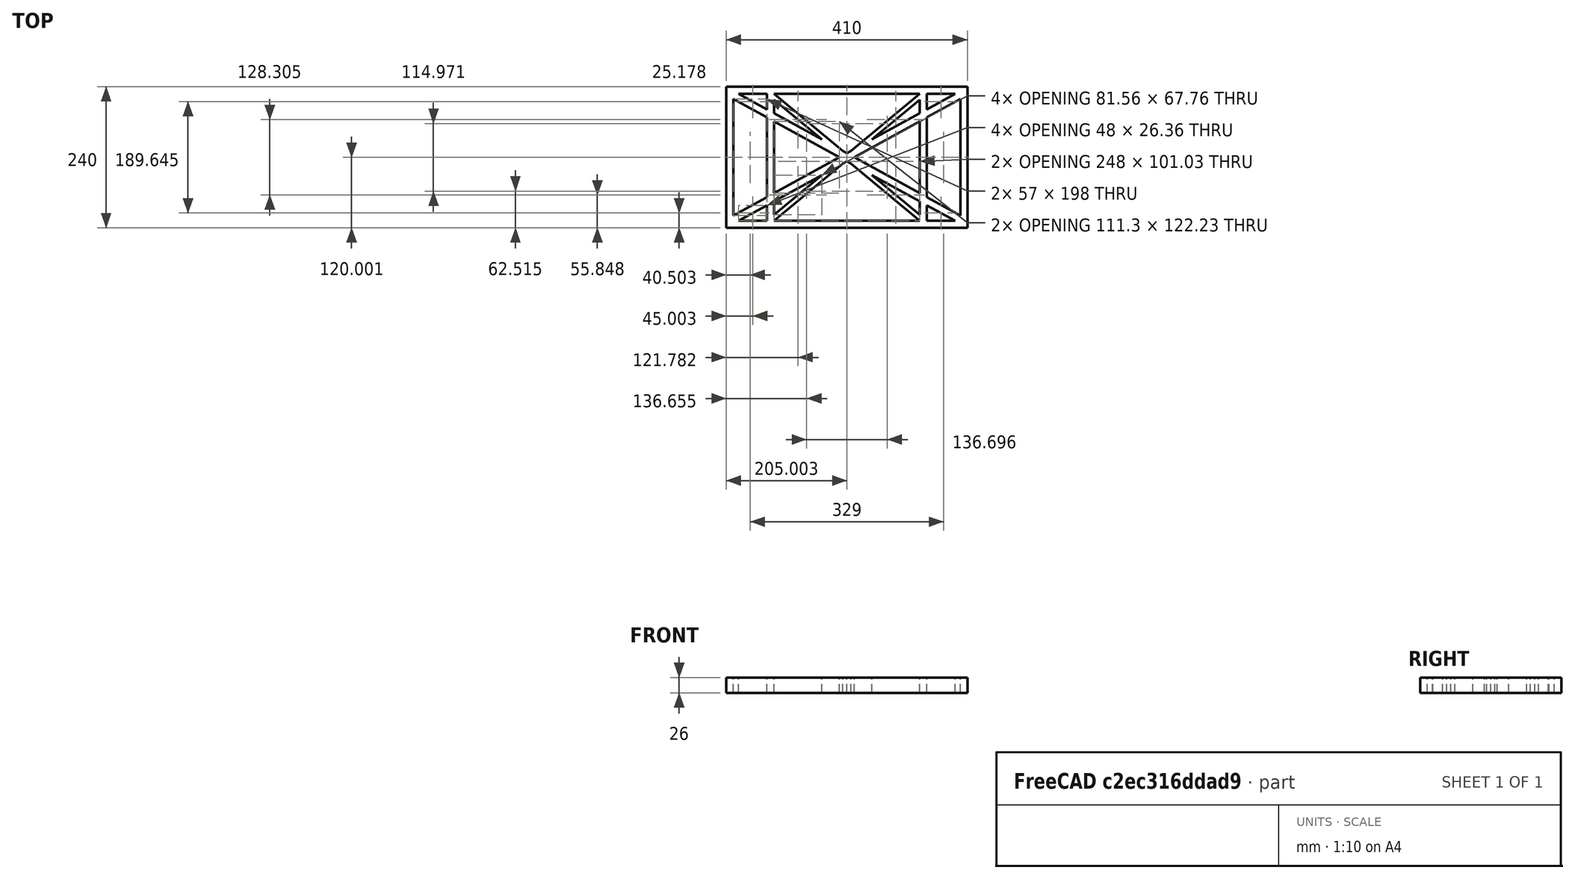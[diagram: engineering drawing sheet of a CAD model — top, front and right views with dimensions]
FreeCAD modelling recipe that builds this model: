
FCSTD DOCUMENT  (FreeCAD 0.19R0.19.2)
Label: laptopStand026
License: All rights reserved
LicenseURL: http://en.wikipedia.org/wiki/All_rights_reserved
objects: Sketcher::SketchObject×3, Part::Extrusion×1
note: 4 computed .brp shape members not serialized (recipe doc carries the construction recipe); baked Part::Feature solids carry a one-line shape summary decoded from their .brp

FEATURE [Sketcher::SketchObject] Sketch
  FullyConstrained = true
  sketch-geometry (52):
    g0: LineSegment StartX=-22.9272 StartY=136.221 StartZ=0 EndX=-22.9272 EndY=-103.779 EndZ=0
    g1: LineSegment StartX=-22.9272 StartY=136.221 StartZ=0 EndX=387.073 EndY=136.221 EndZ=0
    g2: LineSegment StartX=-22.9272 StartY=-103.779 StartZ=0 EndX=387.073 EndY=-103.779 EndZ=0
    g3: LineSegment StartX=387.073 StartY=136.221 StartZ=0 EndX=387.073 EndY=-103.779 EndZ=0
    g4: LineSegment StartX=375.073 StartY=115.221 StartZ=0 EndX=318.073 EndY=83.9235 EndZ=0
    g5: LineSegment StartX=-10.9272 StartY=-82.7794 StartZ=0 EndX=46.0728 EndY=-51.4823 EndZ=0
    g6: LineSegment StartX=-1.92719 StartY=124.221 StartZ=0 EndX=46.0728 EndY=97.8651 EndZ=0
    g7: LineSegment StartX=366.073 StartY=-91.7794 StartZ=0 EndX=318.073 EndY=-65.424 EndZ=0
    g8: LineSegment StartX=-10.9272 StartY=115.221 StartZ=0 EndX=-10.9272 EndY=-82.7794 EndZ=0
    g9: LineSegment StartX=375.073 StartY=-82.7794 StartZ=0 EndX=375.073 EndY=115.221 EndZ=0
    g10: LineSegment StartX=-1.92719 StartY=-91.7794 StartZ=0 EndX=46.0728 EndY=-91.7794 EndZ=0
    g11: LineSegment StartX=318.073 StartY=124.221 StartZ=0 EndX=366.073 EndY=124.221 EndZ=0
    g12: LineSegment StartX=306.073 StartY=-81.8102 StartZ=0 EndX=224.513 EndY=-14.0532 EndZ=0
    g13: LineSegment StartX=58.0728 StartY=114.251 StartZ=0 EndX=139.632 EndY=46.4944 EndZ=0
    g14: LineSegment StartX=306.073 StartY=124.221 StartZ=0 EndX=189.124 EndY=27.0628 EndZ=0
    g15: LineSegment StartX=58.0728 StartY=-91.7794 StartZ=0 EndX=175.022 EndY=5.37834 EndZ=0
    g16: LineSegment StartX=46.0728 StartY=124.221 StartZ=0 EndX=46.0728 EndY=97.8651 EndZ=0
    g17: LineSegment StartX=58.0728 StartY=-81.8102 StartZ=0 EndX=58.0728 EndY=-58.8351 EndZ=0
    g18: LineSegment StartX=318.073 StartY=124.221 StartZ=0 EndX=318.073 EndY=97.8651 EndZ=0
    g19: LineSegment StartX=306.073 StartY=114.251 StartZ=0 EndX=306.073 EndY=91.2763 EndZ=0
    g20: LineSegment StartX=182.073 StartY=23.1914 StartZ=0 EndX=189.124 EndY=27.0628 EndZ=0
    g21: LineSegment StartX=182.073 StartY=9.24976 StartZ=0 EndX=175.022 EndY=5.37834 EndZ=0
    g22: LineSegment StartX=224.513 StartY=46.4944 StartZ=0 EndX=306.073 EndY=114.251 EndZ=0
    g23: LineSegment StartX=175.022 StartY=27.0628 StartZ=0 EndX=58.0728 EndY=124.221 EndZ=0
    g24: LineSegment StartX=169.377 StartY=16.2206 StartZ=0 EndX=58.0728 EndY=77.3346 EndZ=0
    g25: LineSegment StartX=139.632 StartY=-14.0532 StartZ=0 EndX=58.0728 EndY=-81.8102 EndZ=0
    g26: LineSegment StartX=194.768 StartY=16.2206 StartZ=0 EndX=306.073 EndY=-44.8935 EndZ=0
    g27: LineSegment StartX=224.513 StartY=46.4944 StartZ=0 EndX=306.073 EndY=91.2763 EndZ=0
    g28: LineSegment StartX=175.022 StartY=27.0628 StartZ=0 EndX=182.073 EndY=23.1914 EndZ=0
    g29: LineSegment StartX=139.632 StartY=-14.0532 StartZ=0 EndX=58.0728 EndY=-58.8351 EndZ=0
    g30: LineSegment StartX=189.124 StartY=5.37834 StartZ=0 EndX=182.073 EndY=9.24976 EndZ=0
    g31: LineSegment StartX=189.124 StartY=5.37834 StartZ=0 EndX=306.073 EndY=-91.7794 EndZ=0
    g32: LineSegment StartX=306.073 StartY=77.3346 StartZ=0 EndX=306.073 EndY=-44.8935 EndZ=0
    g33: LineSegment StartX=318.073 StartY=83.9235 StartZ=0 EndX=318.073 EndY=-51.4823 EndZ=0
    g34: LineSegment StartX=318.073 StartY=97.8651 StartZ=0 EndX=366.073 EndY=124.221 EndZ=0
    g35: LineSegment StartX=306.073 StartY=77.3346 StartZ=0 EndX=194.768 EndY=16.2206 EndZ=0
    g36: LineSegment StartX=306.073 StartY=-58.8351 StartZ=0 EndX=224.513 EndY=-14.0532 EndZ=0
    g37: LineSegment StartX=306.073 StartY=-58.8351 StartZ=0 EndX=306.073 EndY=-81.8102 EndZ=0
    g38: LineSegment StartX=318.073 StartY=-51.4823 StartZ=0 EndX=375.073 EndY=-82.7794 EndZ=0
    g39: LineSegment StartX=318.073 StartY=-65.424 StartZ=0 EndX=318.073 EndY=-91.7794 EndZ=0
    g40: LineSegment StartX=306.073 StartY=124.221 StartZ=0 EndX=58.0728 EndY=124.221 EndZ=0
    g41: LineSegment StartX=318.073 StartY=-91.7794 StartZ=0 EndX=366.073 EndY=-91.7794 EndZ=0
    g42: LineSegment StartX=58.0728 StartY=-91.7794 StartZ=0 EndX=306.073 EndY=-91.7794 EndZ=0
    g43: LineSegment StartX=58.0728 StartY=-44.8935 StartZ=0 EndX=58.0728 EndY=77.3346 EndZ=0
    g44: LineSegment StartX=46.0728 StartY=-65.424 StartZ=0 EndX=-1.92719 EndY=-91.7794 EndZ=0
    g45: LineSegment StartX=46.0728 StartY=-65.424 StartZ=0 EndX=46.0728 EndY=-91.7794 EndZ=0
    g46: LineSegment StartX=58.0728 StartY=-44.8935 StartZ=0 EndX=169.377 EndY=16.2206 EndZ=0
    g47: LineSegment StartX=58.0728 StartY=91.2763 StartZ=0 EndX=58.0728 EndY=114.251 EndZ=0
    g48: LineSegment StartX=46.0728 StartY=83.9235 StartZ=0 EndX=46.0728 EndY=-51.4823 EndZ=0
    g49: LineSegment StartX=46.0728 StartY=124.221 StartZ=0 EndX=-1.92719 EndY=124.221 EndZ=0
    g50: LineSegment StartX=58.0728 StartY=91.2763 StartZ=0 EndX=139.632 EndY=46.4944 EndZ=0
    g51: LineSegment StartX=46.0728 StartY=83.9235 StartZ=0 EndX=-10.9272 EndY=115.221 EndZ=0
  constraints (102):
    c: Vertical(g0)
    c: Distance(g0) = 240
    c: Horizontal(g1)
    c: Distance(g1) = 410
    c: Coincident(g1,g0)
    c: Coincident(g2,g0)
    c: Horizontal(g2)
    c: Coincident(g3,g1)
    c: Vertical(g3)
    c: Coincident(g2,g3)
    c: Block(g1)
    c: Horizontal(g10)
    c: Horizontal(g11)
    c: PointOnObject(g35,g6)
    c: Coincident(g28,g20)
    c: Coincident(g30,g21)
    c: Tangent(g7,g24)
    c: PointOnObject(g24,g5)
    c: PointOnObject(g26,g4)
    c: Coincident(g20,g14)
    c: Tangent(g20,g27)
    c: Coincident(g50,g13)
    c: Coincident(g28,g23)
    c: Coincident(g22,g27)
    c: Coincident(g21,g15)
    c: Coincident(g29,g25)
    c: Tangent(g21,g29)
    c: Coincident(g36,g12)
    c: Coincident(g31,g30)
    c: Coincident(g22,g19)
    c: Tangent(g19,g32)
    c: Tangent(g18,g33)
    c: Coincident(g27,g19)
    c: Tangent(g27,g34)
    c: Coincident(g4,g33)
    c: Coincident(g35,g32)
    c: Tangent(g4,g35)
    c: Coincident(g37,g12)
    c: Tangent(g7,g36)
    c: Tangent(g32,g37)
    c: Coincident(g26,g32)
    c: Tangent(g26,g38)
    c: Coincident(g33,g38)
    c: Coincident(g39,g7)
    c: Tangent(g33,g39)
    c: Coincident(g25,g17)
    c: Tangent(g17,g43)
    c: Coincident(g29,g17)
    c: Tangent(g29,g44)
    c: Coincident(g45,g44)
    c: Tangent(g16,g45)
    c: Coincident(g5,g48)
    c: Coincident(g46,g43)
    c: Tangent(g5,g46)
    c: Tangent(g43,g47)
    c: Tangent(g16,g48)
    c: Coincident(g13,g47)
    c: PointOnObject(g40,g23)
    c: Tangent(g40,g49)
    c: Coincident(g6,g16)
    c: Coincident(g50,g47)
    c: Tangent(g6,g50)
    c: Coincident(g24,g43)
    c: Coincident(g51,g48)
    c: Tangent(g24,g51)
    c: Block(g23)
    c: Block(g14)
    c: Block(g20)
    c: Block(g40)
    c: Block(g18)
    c: Block(g34)
    c: Block(g4)
    c: Block(g38)
    c: Block(g9)
    c: Block(g36)
    c: Block(g37)
    c: Block(g7)
    c: Block(g39)
    c: Block(g22)
    c: Block(g31)
    c: Block(g42)
    c: Block(g21)
    c: Block(g15)
    c: Block(g29)
    c: Block(g25)
    c: Block(g45)
    c: Block(g44)
    c: Block(g5)
    c: Block(g8)
    c: Block(g51)
    c: Block(g6)
    c: Block(g16)
    c: Block(g13)
    c: Block(g47)
    c: Block(g35)
    c: Block(g32)
    c: Block(g24)
    c: Block(g46)
    c: Block(g49)
    c: Block(g11)
    c: Block(g41)
    c: Block(g10)
FEATURE [Part::Extrusion] Extrude
  Base = -> Sketch
  Dir = (0,0,1)
  DirMode = 2
  FaceMakerClass = Part::FaceMakerBullseye
  LengthFwd = 26
  LengthRev = 0
  Solid = true
  Symmetric = false
FEATURE [Sketcher::SketchObject] Sketch001
  FullyConstrained = false
  MapMode = 4
  Placement = pos=(0,0,0) rot=(0.57735,0.57735,0.57735;2.0944rad)
  Support = -> [Sketch]
  sketch-geometry (43):
    g0: LineSegment StartX=17.2228 StartY=-16.0875 StartZ=0 EndX=117.223 EndY=-16.0875 EndZ=0
    g1: LineSegment StartX=17.2228 StartY=-16.0875 StartZ=0 EndX=17.2228 EndY=-19.0875 EndZ=0
    g2: LineSegment StartX=117.223 StartY=-16.0875 StartZ=0 EndX=117.223 EndY=-19.0875 EndZ=0
    g3: BSplineCurve PolesCount=3 KnotsCount=2 Degree=2 IsPeriodic=0
    g4: LineSegment StartX=94.6577 StartY=-26.1351 StartZ=0 EndX=24.2583 EndY=-213.335 EndZ=0
    g5: LineSegment StartX=-9.4377 StartY=-200.664 StartZ=0 EndX=24.2583 EndY=-213.335 EndZ=0
    g6: LineSegment StartX=-9.4377 StartY=-200.664 StartZ=0 EndX=56.1962 EndY=-26.1351 EndZ=0
    g7: LineSegment StartX=17.2228 StartY=-19.0875 StartZ=0 EndX=38.8094 EndY=-19.0875 EndZ=0
    g8: BSplineCurve PolesCount=4 KnotsCount=2 Degree=3 IsPeriodic=0
    g9: LineSegment StartX=78.0148 StartY=-19.2805 StartZ=0 EndX=73.122 EndY=-32.2909 EndZ=0
    g10: ArcOfCircle CenterX=73.122 CenterY=-32.2909 CenterZ=0 NormalX=0 NormalY=0 NormalZ=1 AngleXU=0 Radius=13 StartAngle=5.92268 EndAngle=9.06428
    g11: LineSegment StartX=73.122 StartY=-32.2909 StartZ=0 EndX=77.698 EndY=-20.1229 EndZ=0
    g12: LineSegment StartX=73.122 StartY=-32.2909 StartZ=0 EndX=65.1306 EndY=-53.8393 EndZ=0
    g13: LineSegment StartX=65.1306 StartY=-53.8393 StartZ=0 EndX=62.3064 EndY=-61.3494 EndZ=0
    g14: LineSegment StartX=85.2864 StartY=-36.8765 StartZ=0 EndX=78.9505 EndY=-53.7246 EndZ=0
    g15: LineSegment StartX=60.9577 StartY=-27.7052 StartZ=0 EndX=54.6191 EndY=-44.5532 EndZ=0
    g16: ArcOfCircle CenterX=66.7816 CenterY=-49.1439 CenterZ=0 NormalX=0 NormalY=0 NormalZ=1 AngleXU=0 Radius=13 StartAngle=2.78068 EndAngle=5.92131
    g17: ArcOfCircle CenterX=97.2888 CenterY=-81.8271 CenterZ=0 NormalX=0 NormalY=0 NormalZ=1 AngleXU=0 Radius=13 StartAngle=5.92268 EndAngle=9.06428
    g18: LineSegment StartX=101.865 StartY=-69.6591 StartZ=0 EndX=97.2888 EndY=-81.8271 EndZ=0
    g19: LineSegment StartX=85.1244 StartY=-77.2415 StartZ=0 EndX=78.7885 EndY=-94.0895 EndZ=0
    g20: ArcOfCircle CenterX=90.9509 CenterY=-98.6802 CenterZ=0 NormalX=0 NormalY=0 NormalZ=1 AngleXU=0 Radius=13 StartAngle=2.78068 EndAngle=5.92131
    g21: LineSegment StartX=109.453 StartY=-86.4128 StartZ=0 EndX=103.117 EndY=-103.261 EndZ=0
    g22: ArcOfCircle CenterX=34.6196 CenterY=-134.619 CenterZ=0 NormalX=0 NormalY=0 NormalZ=1 AngleXU=0 Radius=13 StartAngle=5.92268 EndAngle=9.06428
    g23: LineSegment StartX=22.4552 StartY=-130.033 StartZ=0 EndX=16.1193 EndY=-146.881 EndZ=0
    g24: ArcOfCircle CenterX=28.2818 CenterY=-151.472 CenterZ=0 NormalX=0 NormalY=0 NormalZ=1 AngleXU=0 Radius=13 StartAngle=2.78068 EndAngle=5.92131
    g25: LineSegment StartX=46.784 StartY=-139.204 StartZ=0 EndX=40.448 EndY=-156.052 EndZ=0
    g26: LineSegment StartX=39.1956 StartY=-122.451 StartZ=0 EndX=34.6196 EndY=-134.619 EndZ=0
    g27: LineSegment StartX=34.6196 StartY=-134.619 StartZ=0 EndX=23.7058 EndY=-163.64 EndZ=0
    g28: LineSegment StartX=23.7058 StartY=-163.64 StartZ=0 EndX=19.9535 EndY=-173.618 EndZ=0
    g29: LineSegment StartX=62.3064 StartY=-61.3494 StartZ=0 EndX=60.5464 EndY=-66.0294 EndZ=0
    g30: ArcOfCircle CenterX=55.9263 CenterY=-78.1807 CenterZ=0 NormalX=0 NormalY=0 NormalZ=1 AngleXU=0 Radius=13 StartAngle=5.92268 EndAngle=9.06428
    g31: LineSegment StartX=68.0907 StartY=-82.7664 StartZ=0 EndX=61.7547 EndY=-99.6148 EndZ=0
    g32: ArcOfCircle CenterX=49.5884 CenterY=-95.0342 CenterZ=0 NormalX=0 NormalY=0 NormalZ=1 AngleXU=0 Radius=13 StartAngle=2.78068 EndAngle=5.92131
    g33: LineSegment StartX=43.7619 StartY=-73.595 StartZ=0 EndX=37.426 EndY=-90.4435 EndZ=0
    g34: LineSegment StartX=45.0565 StartY=-107.219 StartZ=0 EndX=43.2966 EndY=-111.899 EndZ=0
    g35: LineSegment StartX=60.5464 StartY=-66.0294 StartZ=0 EndX=45.0565 EndY=-107.219 EndZ=0
    g36: ArcOfCircle CenterX=38.7206 CenterY=-124.067 CenterZ=0 NormalX=0 NormalY=0 NormalZ=1 AngleXU=0 Radius=13 StartAngle=5.92268 EndAngle=9.06428
    g37: LineSegment StartX=26.5562 StartY=-119.481 StartZ=0 EndX=20.2203 EndY=-136.329 EndZ=0
    g38: ArcOfCircle CenterX=32.3828 CenterY=-140.92 CenterZ=0 NormalX=0 NormalY=0 NormalZ=1 AngleXU=0 Radius=13 StartAngle=2.78068 EndAngle=5.92131
    g39: LineSegment StartX=50.885 StartY=-128.652 StartZ=0 EndX=44.549 EndY=-145.5 EndZ=0
    g40: LineSegment StartX=38.7206 StartY=-124.067 StartZ=0 EndX=27.8068 EndY=-153.088 EndZ=0
    g41: LineSegment StartX=27.8068 StartY=-153.088 StartZ=0 EndX=24.0545 EndY=-163.066 EndZ=0
    g42: LineSegment StartX=43.2966 StartY=-111.899 StartZ=0 EndX=38.7206 EndY=-124.067 EndZ=0
  constraints (87):
    c: Horizontal(g0)
    c: Distance(g0) = 100
    c: Block(g0)
    c: Coincident(g1,g0)
    c: Vertical(g1)
    c: Distance(g1) = 3
    c: Coincident(g2,g0)
    c: Vertical(g2)
    c: Distance(g2) = 3
    c: Block(g3)
    c: Coincident(g3,g2)
    c: Coincident(g4,g3)
    c: Block(g4)
    c: Coincident(g5,g4)
    c: Coincident(g6,g5)
    c: Coincident(g7,g1)
    c: Horizontal(g7)
    c: Block(g8)
    c: Coincident(g8,g7)
    c: Coincident(g8,g6)
    c: Block(g6)
    c: Block(g10)
    c: Coincident(g11,g10)
    c: PointOnObject(g11,g10)
    c: Coincident(g11,g9)
    c: Block(g9)
    c: Coincident(g12,g9)
    c: Coincident(g13,g12)
    c: Parallel(g4,g13)
    c: Distance(g14) = 18
    c: Coincident(g14,g10)
    c: Parallel(g4,g14)
    c: Coincident(g15,g10)
    c: Block(g16)
    c: Coincident(g16,g15)
    c: Block(g15)
    c: Equal(g14,g21) = 18
    c: Coincident(g21,g17)
    c: Coincident(g19,g17)
    c: Block(g20)
    c: Coincident(g20,g19)
    c: Block(g19)
    c: PointOnObject(g13,g16)
    c: Block(g17)
    c: PointOnObject(g18,g17)
    c: Coincident(g25,g22)
    c: Coincident(g23,g22)
    c: Block(g24)
    c: Coincident(g24,g23)
    c: Block(g23)
    c: Block(g22)
    c: PointOnObject(g26,g22)
    c: Coincident(g27,g22)
    c: Parallel(g4,g27)
    c: PointOnObject(g27,g24)
    c: Coincident(g28,g27)
    c: Distance(g28) = 10.66
    c: Parallel(g4,g28)
    c: Distance(g29) = 5
    c: Parallel(g4,g29)
    c: Coincident(g29,g13)
    c: Coincident(g31,g30)
    c: Coincident(g33,g30)
    c: Block(g32)
    c: Coincident(g32,g33)
    c: Block(g33)
    c: Block(g30)
    c: PointOnObject(g29,g30)
    c: Block(g31)
    c: Distance(g34) = 5
    c: Parallel(g4,g34)
    c: Coincident(g35,g29)
    c: Parallel(g4,g35)
    c: PointOnObject(g35,g32)
    c: Coincident(g34,g35)
    c: Coincident(g39,g36)
    c: Coincident(g37,g36)
    c: Block(g38)
    c: Coincident(g38,g37)
    c: Block(g37)
    c: Block(g36)
    c: PointOnObject(g42,g36)
    c: Coincident(g40,g36)
    c: PointOnObject(g40,g38)
    c: Coincident(g41,g40)
    c: Equal(g28,g41) = 10.66
    c: Coincident(g42,g34)
FEATURE [Sketcher::SketchObject] Sketch002
  FullyConstrained = true
  Placement = pos=(0,0,0) rot=(-1,0,0;4.71239rad)
